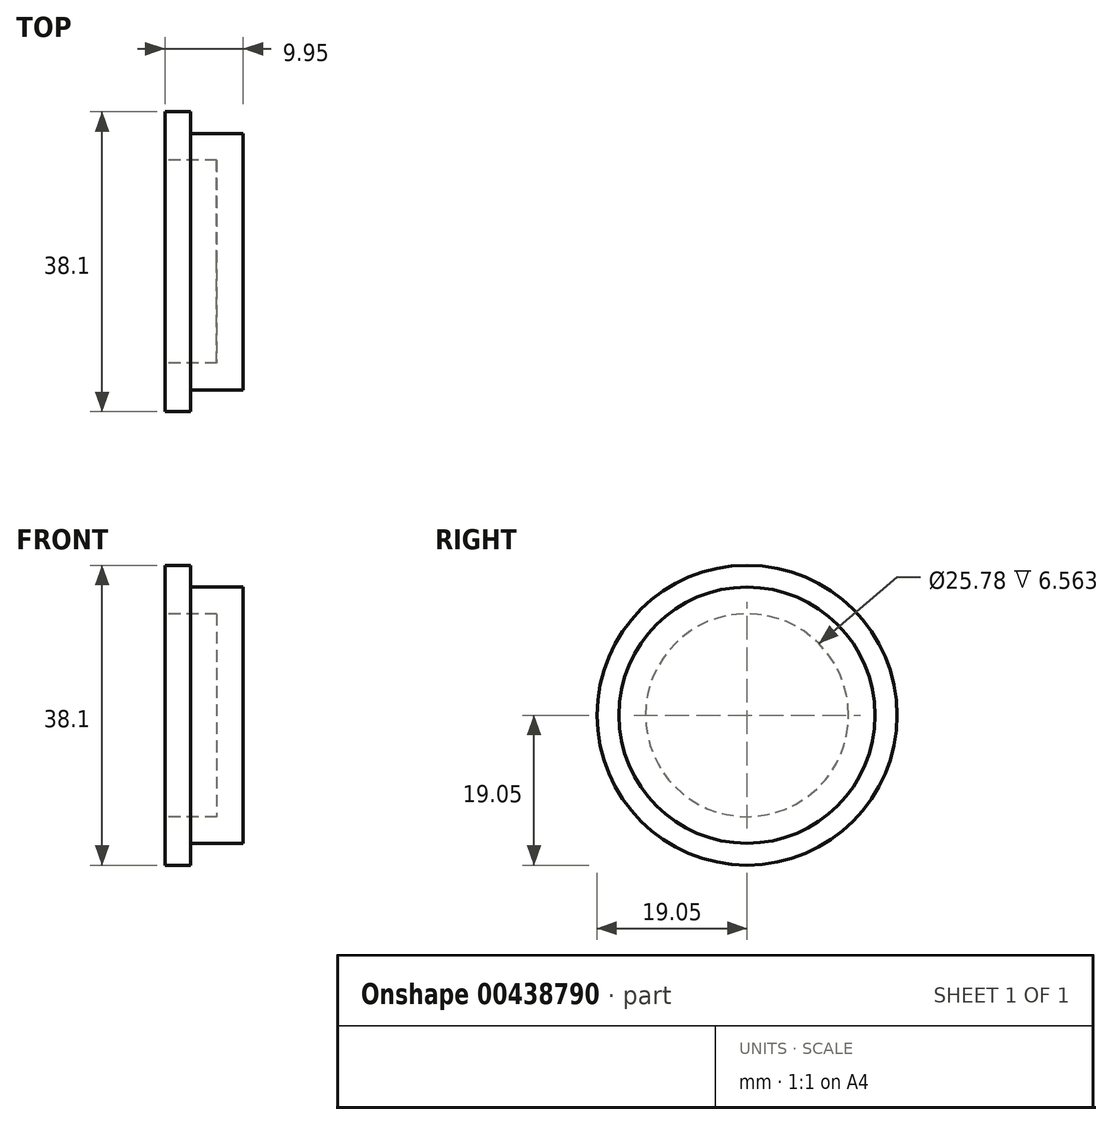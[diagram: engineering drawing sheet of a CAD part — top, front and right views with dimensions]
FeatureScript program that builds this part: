
annotation { "Feature Type Name" : "Feature", "Feature Type Description" : "" }
export const myFeature = defineFeature(function(context is Context, id is Id, definition is map)
    precondition{}
    {
        {
            var Q0;
            Q0=qCreatedBy(makeId("Front.planeOp"),FACE);
            var sketch = newSketch(context, id + "F0", { "sketchPlane" : qUnion([Q0])});
            skLineSegment(sketch, "E0", {"start": v(0, 19.05) * mm, "end": v(-3.28, 19.05) * mm});
            skLineSegment(sketch, "E1", {"start": v(-3.28, 19.05) * mm, "end": v(-3.28, 12.9) * mm});
            skLineSegment(sketch, "E2", {"start": v(-3.28, 12.9) * mm, "end": v(3.29, 12.9) * mm});
            skLineSegment(sketch, "E3", {"start": v(6.67, 0) * mm, "end": v(6.67, 16.27) * mm});
            skLineSegment(sketch, "E4", {"start": v(6.67, 16.27) * mm, "end": v(0, 16.27) * mm});
            skLineSegment(sketch, "E5", {"start": v(0, 16.27) * mm, "end": v(0, 19.05) * mm});
            skLineSegment(sketch, "E6", {"start": v(-10.27, 0) * mm, "end": v(11.51, 0) * mm, "construction": true});
            skLineSegment(sketch, "E7", {"start": v(6.67, 0) * mm, "end": v(3.29, 0) * mm});
            skLineSegment(sketch, "E8", {"start": v(3.29, 0) * mm, "end": v(3.29, 12.9) * mm});
            skSolve(sketch);
        }
        {
            var Q0;
            Q0 = qSketchRegion(id + "F0", true);
            var Q1;
            Q1=sQuery(id+"F0.wireOp",EDGE,"E6");
            revolve(context, id + "F1", {"entities" : qUnion([Q0]), "axis" : qUnion([Q1]), "revolveType" : RevolveType.FULL});
        }
    });
